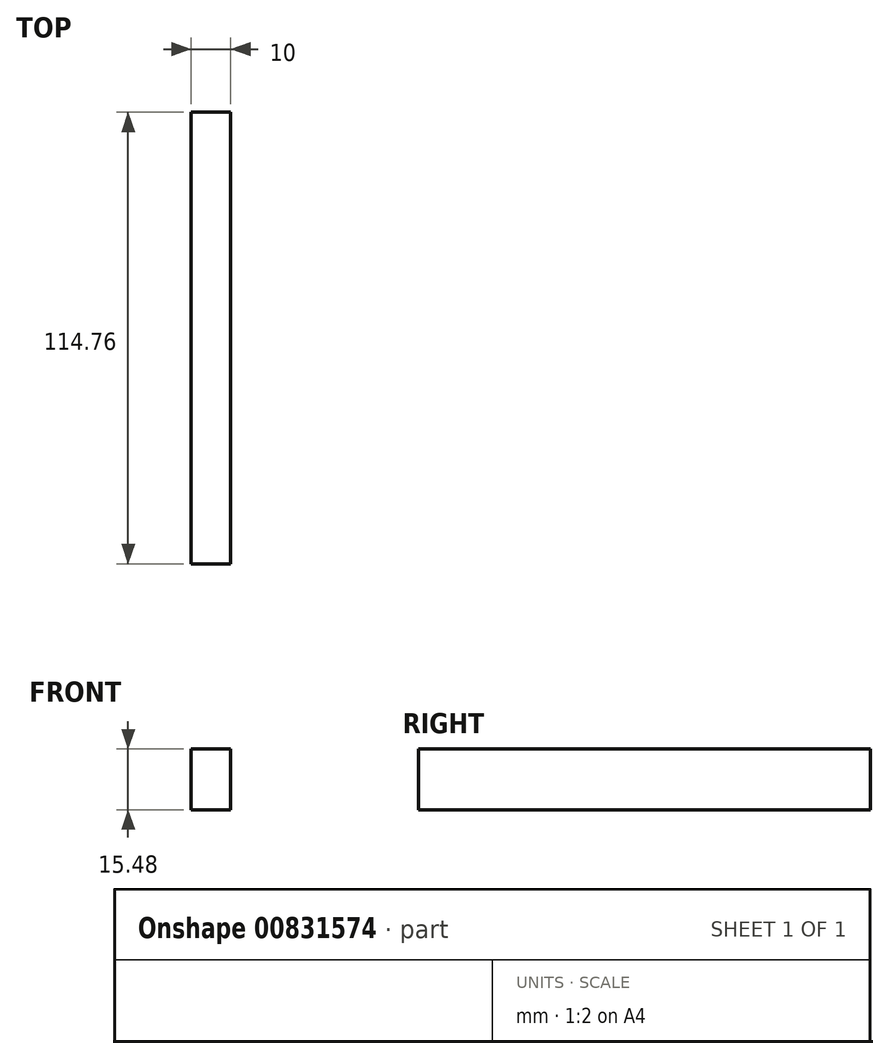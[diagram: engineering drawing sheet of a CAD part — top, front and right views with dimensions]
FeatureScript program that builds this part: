
annotation { "Feature Type Name" : "Feature", "Feature Type Description" : "" }
export const myFeature = defineFeature(function(context is Context, id is Id, definition is map)
    precondition{}
    {
        {
            var Q0;
            Q0=qCreatedBy(makeId("Right.planeOp"),FACE);
            var sketch = newSketch(context, id + "F0", { "sketchPlane" : qUnion([Q0])});
            skLineSegment(sketch, "E0.bottom", {"start": v(-57.38, 7.74) * mm, "end": v(57.38, 7.74) * mm});
            skLineSegment(sketch, "E0.top", {"start": v(-57.38, -7.74) * mm, "end": v(57.38, -7.74) * mm});
            skLineSegment(sketch, "E0.left", {"start": v(-57.38, 7.74) * mm, "end": v(-57.38, -7.74) * mm});
            skLineSegment(sketch, "E0.right", {"start": v(57.38, 7.74) * mm, "end": v(57.38, -7.74) * mm});
            skPoint(sketch, "E0.middle", {"position": v(0, 0) * mm});
            skSolve(sketch);
        }
        {
            var Q0;
            Q0 = qSketchRegion(id + "F0", true);
            extrude(context, id + "F1", {"entities" : qUnion([Q0]), "depth" : 10 * mm, "offsetDistance" : 25.4 * mm});
        }
    });
